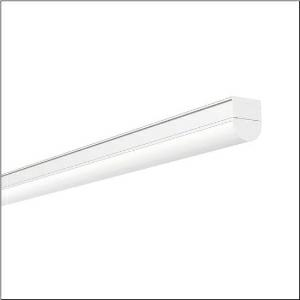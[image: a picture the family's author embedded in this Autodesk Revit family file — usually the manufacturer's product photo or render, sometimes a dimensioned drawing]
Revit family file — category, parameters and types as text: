
# Revit family: ecopack_r__31_51lj12mdm20a_29c1
name_source: partatom
category: Lighting Fixtures
units: mm (PartAtom-declared; Revit-internal decimal feet)

## family parameters
Cut with Voids When Loaded = No
Host = Face
Light Source = No
Part Type = Normal
Room Calculation Point = No
Round Connector Dimension = Use Diameter
Shared = No

## types (1)
- --- (1 x LED, 2510 lm, 20 W, 5000K)
    Apparent Load = 20 VA
    CIE Flux Codes = 41 71 90 93 100
    Color Rendering = 80
    Color Temperature = 5000K
    Default Elevation = 1800 mm
    Description = Ecopack® 31, diffuser luminaire, primary optical cover: cover, of PC, frosted, light emission: direct distribution, primary light characteristic: symmetric, installation type: surface-mounted, LED, rated luminous flux: 2.600lm, luminous efficacy: 130lm/W, light colour: 830/840/850, colour temperature: 3000/4000/5000K, control gear: ECG, with terminal, 3-pole, mains connection: 220..240V, AC, 50/60Hz, rated input power: 20W, housing, of aluminium, traffic white (RAL 9016), length: 600mm, width: 56mm, height: 68mm, end cap, of PC, white, protection rating (complete): IP20, insulation class (complete): insulation class I (protective earthing), certification: CE, impact resistance: IK06, permissible operating ambient temperature: -20..+40°C, packaging unit: 1 piece
    Height = 68 mm
    Lamp = 1 x LED
    Lamp Light Flux = 2510 lm
    Lamp Power = 20 W
    Lamp count = 1
    Length = 600 mm
    Luminous efficacy = 126 lm/W
    Manufacturer = Siteco
    ModVariant = No
    Model = 51LJ12MDM20A
    Mounting Place = Ceiling
    Mounting Type = Surface mounted
    Number of Poles = 1
    OnlyDefault = Yes
    Power Factor = 1
    Product Name = Ecopack® 31
    Product group = diffuser luminaire
    ProductGroupID = 303
    Protection Class = Protection class I
    Protection Degree = IP 20
    RLX_Detail_Level = 1
    RlxData = <blob elided: 25841 chars, md5=00fecb7e>
    Socket = socket
    Standby Power = 0 W
    System Light Flux = 2510 lm
    System Power = 20 W
    Type Comments = individual setting: colour temperature 5000K, luminous flux: 100 % | (ON | ON)
    Type Image = l_1007030.jpg
    URL = http://relux.com
    VarID = @adj_086381
    Voltage = 0 V
    Weight = 0.00 kg
    Width = 56 mm

## geometry (parser evidence)
native form markers: Blend x4, Sweep x13
no freeform markers — native parametric forms only
